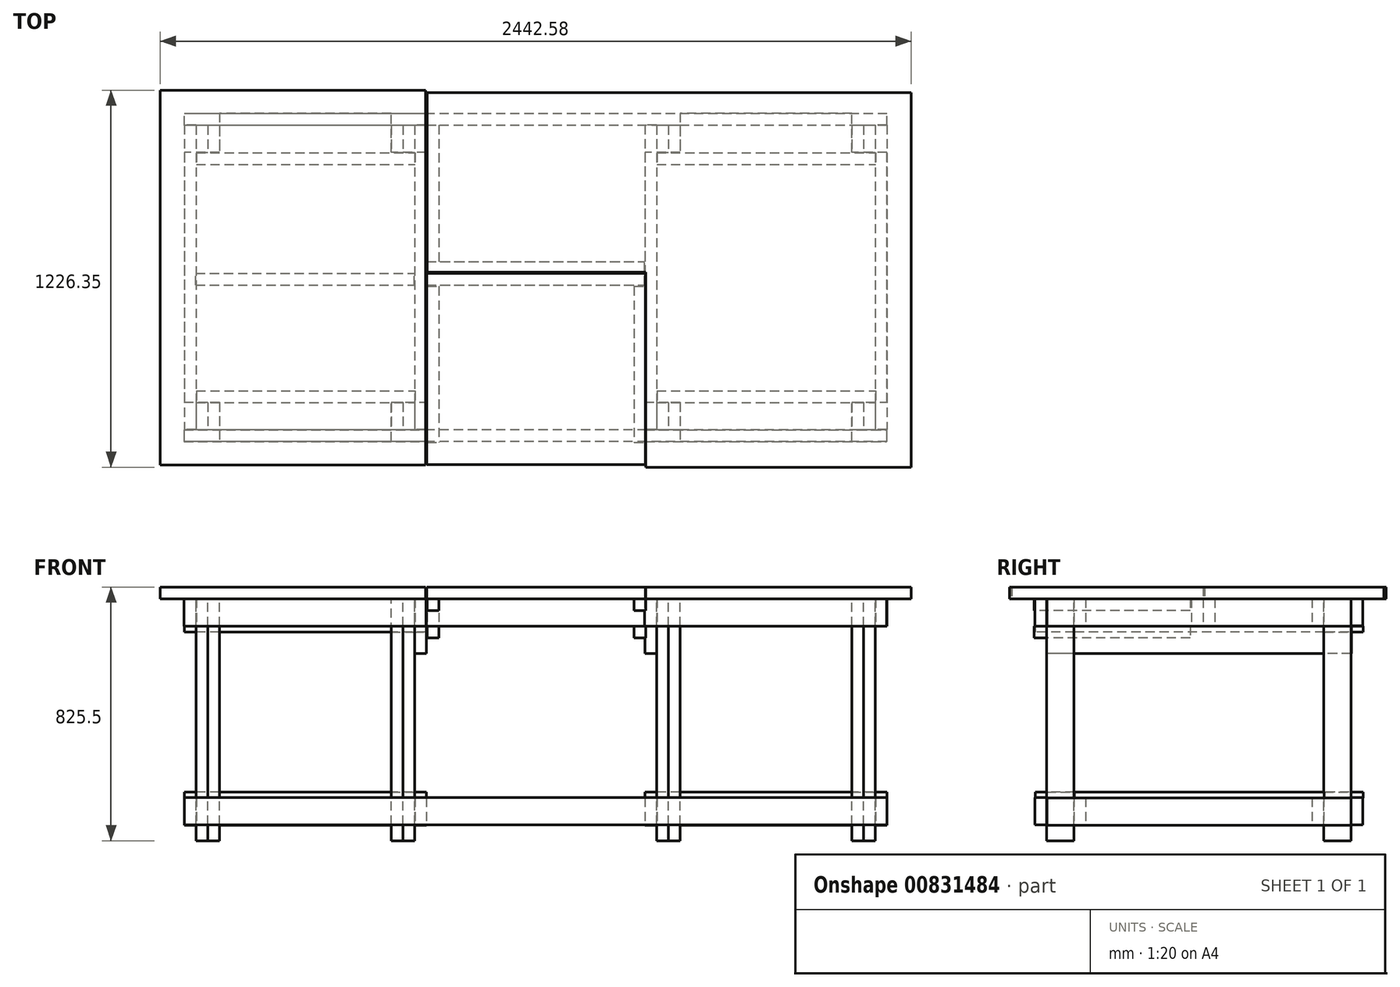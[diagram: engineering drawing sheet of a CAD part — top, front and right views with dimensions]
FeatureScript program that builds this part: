
annotation { "Feature Type Name" : "Feature", "Feature Type Description" : "" }
export const myFeature = defineFeature(function(context is Context, id is Id, definition is map)
    precondition{}
    {
        {
            var Q0;
            Q0=qCreatedBy(makeId("Top.planeOp"),FACE);
            var sketch = newSketch(context, id + "F0", { "sketchPlane" : qUnion([Q0])});
            skLineSegment(sketch, "E0.bottom", {"start": v(-393.7, 19.05) * mm, "end": v(393.7, 19.05) * mm});
            skLineSegment(sketch, "E0.top", {"start": v(-393.7, -19.05) * mm, "end": v(393.7, -19.05) * mm});
            skLineSegment(sketch, "E0.left", {"start": v(-393.7, 19.05) * mm, "end": v(-393.7, -19.05) * mm});
            skLineSegment(sketch, "E0.right", {"start": v(393.7, 19.05) * mm, "end": v(393.7, -19.05) * mm});
            skPoint(sketch, "E0.middle", {"position": v(0, 0) * mm});
            skSolve(sketch);
        }
        {
            var Q0;
            Q0=makeQuery(id+"F0.imprint","IMPRINT",FACE,{"disambiguationData":[TD([[makeQuery(id+"F0.imprint","IMPRINT",EDGE,{"derivedFrom":sQuery(id+"F0.wireOp",EDGE,"E0.bottom")}),-1.0]])]});
            extrude(context, id + "F1", {"entities" : qUnion([Q0]), "depth" : 88.9 * mm, "offsetDistance" : 25.4 * mm});
        }
        {
            var Q0;
            Q0=makeQuery(id+"F1.opExtrude","SWEPT_BODY",BODY,{"disambiguationData":[OSD([sQuery(id+"F0.wireOp",EDGE,"E0.bottom"),sQuery(id+"F0.wireOp",EDGE,"E0.top"),sQuery(id+"F0.wireOp",EDGE,"E0.left"),sQuery(id+"F0.wireOp",EDGE,"E0.right")])]});
            var Q1;
            Q1=qCreatedBy(makeId("Front.planeOp"),FACE);
            transform(context, id + "F2", {"entities" : qUnion([Q0]), "transformType" : TransformType.TRANSLATION_DISTANCE, "transformDirection" : qUnion([Q1]), "distance" : 1028.7 * mm, "makeCopy" : true});
        }
        {
            var Q0;
            Q0=makeQuery(id+"F1.opExtrude","SWEPT_BODY",BODY,{"disambiguationData":[OSD([sQuery(id+"F0.wireOp",EDGE,"E0.bottom"),sQuery(id+"F0.wireOp",EDGE,"E0.top"),sQuery(id+"F0.wireOp",EDGE,"E0.left"),sQuery(id+"F0.wireOp",EDGE,"E0.right")])]});
            var Q1;
            Q1=makeQuery(id+"F1.opExtrude","SWEPT_FACE",FACE,{"disambiguationData":[OSD([sQuery(id+"F0.wireOp",EDGE,"E0.right")])]});
            transform(context, id + "F3", {"entities" : qUnion([Q0]), "transformType" : TransformType.TRANSLATION_DISTANCE, "transformDirection" : qUnion([Q1]), "distance" : 1498.6 * mm, "makeCopy" : true});
        }
        {
            var Q0;
            Q0=makeQuery(id+"F3.opPattern","COPY",EDGE,{"derivedFrom":makeQuery(id+"F1.opExtrude","CAP_EDGE",EDGE,{"disambiguationData":[OSD([sQuery(id+"F0.wireOp",EDGE,"E0.top")])],"isStart":true}),"instanceName":"1"});
            cPoint(context, id + "F4", {"entities" : qUnion([Q0]), "parameter" : 0.5});
        }
        {
            var Q0;
            Q0=makeQuery(id+"F3.opPattern","COPY",BODY,{"derivedFrom":makeQuery(id+"F1.opExtrude","SWEPT_BODY",BODY,{"disambiguationData":[OSD([sQuery(id+"F0.wireOp",EDGE,"E0.bottom"),sQuery(id+"F0.wireOp",EDGE,"E0.top"),sQuery(id+"F0.wireOp",EDGE,"E0.left"),sQuery(id+"F0.wireOp",EDGE,"E0.right")])]}),"instanceName":"1"});
            var Q1;
            Q1 = qCreatedBy(id + "F4" ,VERTEX);
            var Q2;
            Q2=makeQuery(id+"F3.opPattern","COPY",EDGE,{"derivedFrom":makeQuery(id+"F1.opExtrude","CAP_EDGE",EDGE,{"disambiguationData":[OSD([sQuery(id+"F0.wireOp",EDGE,"E0.top")])],"isStart":false}),"instanceName":"1"});
            var Q3;
            Q3=makeQuery(id+"F3.opPattern","COPY",FACE,{"derivedFrom":makeQuery(id+"F1.opExtrude","SWEPT_FACE",FACE,{"disambiguationData":[OSD([sQuery(id+"F0.wireOp",EDGE,"E0.top")])]}),"instanceName":"1"});
            transform(context, id + "F5", {"entities" : qUnion([Q0]), "transformType" : TransformType.TRANSLATION_DISTANCE, "transformDirection" : qUnion([Q3]), "distance" : 1028.7 * mm, "makeCopy" : true});
        }
        {
            var Q0;
            Q0=qCreatedBy(makeId("Top.planeOp"),FACE);
            var sketch = newSketch(context, id + "F6", { "sketchPlane" : qUnion([Q0])});
            skLineSegment(sketch, "E1.bottom", {"start": v(1892.74, -19.08) * mm, "end": v(1854.64, -19.08) * mm});
            skLineSegment(sketch, "E1.top", {"start": v(1892.74, -107.98) * mm, "end": v(1854.64, -107.98) * mm});
            skLineSegment(sketch, "E1.left", {"start": v(1892.74, -19.08) * mm, "end": v(1892.74, -107.98) * mm});
            skLineSegment(sketch, "E1.right", {"start": v(1854.64, -19.08) * mm, "end": v(1854.64, -107.98) * mm});
            skSolve(sketch);
        }
        {
            var Q0;
            Q0=makeQuery(id+"F6.imprint","IMPRINT",FACE,{"disambiguationData":[TD([[makeQuery(id+"F6.imprint","IMPRINT",EDGE,{"derivedFrom":sQuery(id+"F6.wireOp",EDGE,"E1.bottom")}),1.0]])]});
            extrude(context, id + "F7", {"entities" : qUnion([Q0]), "oppositeDirection" : true, "depth" : 698.5 * mm, "offsetDistance" : 25.4 * mm, "hasSecondDirection" : true, "secondDirectionOppositeDirection" : false, "secondDirectionDepth" : 88.9 * mm});
        }
        {
            var Q0;
            Q0=makeQuery(id+"F7.opExtrude","SWEPT_BODY",BODY,{"disambiguationData":[OSD([sQuery(id+"F6.wireOp",EDGE,"E1.bottom"),sQuery(id+"F6.wireOp",EDGE,"E1.top"),sQuery(id+"F6.wireOp",EDGE,"E1.left"),sQuery(id+"F6.wireOp",EDGE,"E1.right")])]});
            var Q1;
            Q1=makeQuery(id+"F7.opExtrude","SWEPT_FACE",FACE,{"disambiguationData":[OSD([sQuery(id+"F6.wireOp",EDGE,"E1.top")])]});
            var Q2;
            Q2=makeQuery(id+"F7.opExtrude","SWEPT_FACE",FACE,{"disambiguationData":[OSD([sQuery(id+"F6.wireOp",EDGE,"E1.left")])]});
            transform(context, id + "F8", {"entities" : qUnion([Q0]), "transformType" : TransformType.TRANSLATION_DISTANCE, "transformDirection" : qUnion([Q1, Q2]), "distance" : 901.7 * mm, "makeCopy" : true});
        }
        {
            var Q0;
            Q0=makeQuery(id+"F8.opPattern","COPY",BODY,{"derivedFrom":makeQuery(id+"F7.opExtrude","SWEPT_BODY",BODY,{"disambiguationData":[OSD([sQuery(id+"F6.wireOp",EDGE,"E1.bottom"),sQuery(id+"F6.wireOp",EDGE,"E1.top"),sQuery(id+"F6.wireOp",EDGE,"E1.left"),sQuery(id+"F6.wireOp",EDGE,"E1.right")])]}),"instanceName":"1"});
            var Q1;
            Q1=makeQuery(id+"F8.opPattern","COPY",FACE,{"derivedFrom":makeQuery(id+"F7.opExtrude","SWEPT_FACE",FACE,{"disambiguationData":[OSD([sQuery(id+"F6.wireOp",EDGE,"E1.right")])]}),"instanceName":"1"});
            transform(context, id + "F9", {"entities" : qUnion([Q0]), "transformType" : TransformType.TRANSLATION_DISTANCE, "transformDirection" : qUnion([Q1]), "distance" : 749.3 * mm, "makeCopy" : true});
        }
        {
            var Q0;
            Q0=makeQuery(id+"F7.opExtrude","SWEPT_BODY",BODY,{"disambiguationData":[OSD([sQuery(id+"F6.wireOp",EDGE,"E1.bottom"),sQuery(id+"F6.wireOp",EDGE,"E1.top"),sQuery(id+"F6.wireOp",EDGE,"E1.left"),sQuery(id+"F6.wireOp",EDGE,"E1.right")])]});
            var Q1;
            Q1=makeQuery(id+"F7.opExtrude","SWEPT_FACE",FACE,{"disambiguationData":[OSD([sQuery(id+"F6.wireOp",EDGE,"E1.right")])]});
            transform(context, id + "F10", {"entities" : qUnion([Q0]), "transformType" : TransformType.TRANSLATION_DISTANCE, "transformDirection" : qUnion([Q1]), "distance" : 749.3 * mm, "makeCopy" : true});
        }
        {
            var Q0;
            Q0=makeQuery(id+"F10.opPattern","COPY",BODY,{"derivedFrom":makeQuery(id+"F7.opExtrude","SWEPT_BODY",BODY,{"disambiguationData":[OSD([sQuery(id+"F6.wireOp",EDGE,"E1.bottom"),sQuery(id+"F6.wireOp",EDGE,"E1.top"),sQuery(id+"F6.wireOp",EDGE,"E1.left"),sQuery(id+"F6.wireOp",EDGE,"E1.right")])]}),"instanceName":"1"});
            var Q1;
            Q1=makeQuery(id+"F10.opPattern","COPY",FACE,{"derivedFrom":makeQuery(id+"F7.opExtrude","SWEPT_FACE",FACE,{"disambiguationData":[OSD([sQuery(id+"F6.wireOp",EDGE,"E1.right")])]}),"instanceName":"1"});
            transform(context, id + "F11", {"entities" : qUnion([Q0]), "transformType" : TransformType.TRANSLATION_DISTANCE, "transformDirection" : qUnion([Q1]), "distance" : 749.3 * mm, "makeCopy" : true});
        }
        {
            var Q0;
            Q0=makeQuery(id+"F9.opPattern","COPY",BODY,{"derivedFrom":makeQuery(id+"F8.opPattern","COPY",BODY,{"derivedFrom":makeQuery(id+"F7.opExtrude","SWEPT_BODY",BODY,{"disambiguationData":[OSD([sQuery(id+"F6.wireOp",EDGE,"E1.bottom"),sQuery(id+"F6.wireOp",EDGE,"E1.top"),sQuery(id+"F6.wireOp",EDGE,"E1.left"),sQuery(id+"F6.wireOp",EDGE,"E1.right")])]}),"instanceName":"1"}),"instanceName":"1"});
            var Q1;
            Q1=makeQuery(id+"F9.opPattern","COPY",FACE,{"derivedFrom":makeQuery(id+"F8.opPattern","COPY",FACE,{"derivedFrom":makeQuery(id+"F7.opExtrude","SWEPT_FACE",FACE,{"disambiguationData":[OSD([sQuery(id+"F6.wireOp",EDGE,"E1.right")])]}),"instanceName":"1"}),"instanceName":"1"});
            transform(context, id + "F12", {"entities" : qUnion([Q0]), "transformType" : TransformType.TRANSLATION_DISTANCE, "transformDirection" : qUnion([Q1]), "distance" : 749.3 * mm, "makeCopy" : true});
        }
        {
            var Q0;
            Q0=makeQuery(id+"F12.opPattern","COPY",BODY,{"derivedFrom":makeQuery(id+"F9.opPattern","COPY",BODY,{"derivedFrom":makeQuery(id+"F8.opPattern","COPY",BODY,{"derivedFrom":makeQuery(id+"F7.opExtrude","SWEPT_BODY",BODY,{"disambiguationData":[OSD([sQuery(id+"F6.wireOp",EDGE,"E1.bottom"),sQuery(id+"F6.wireOp",EDGE,"E1.top"),sQuery(id+"F6.wireOp",EDGE,"E1.left"),sQuery(id+"F6.wireOp",EDGE,"E1.right")])]}),"instanceName":"1"}),"instanceName":"1"}),"instanceName":"1"});
            var Q1;
            Q1=makeQuery(id+"F12.opPattern","COPY",FACE,{"derivedFrom":makeQuery(id+"F9.opPattern","COPY",FACE,{"derivedFrom":makeQuery(id+"F8.opPattern","COPY",FACE,{"derivedFrom":makeQuery(id+"F7.opExtrude","SWEPT_FACE",FACE,{"disambiguationData":[OSD([sQuery(id+"F6.wireOp",EDGE,"E1.right")])]}),"instanceName":"1"}),"instanceName":"1"}),"instanceName":"1"});
            transform(context, id + "F13", {"entities" : qUnion([Q0]), "transformType" : TransformType.TRANSLATION_DISTANCE, "transformDirection" : qUnion([Q1]), "distance" : 749.3 * mm, "makeCopy" : true});
        }
        {
            var Q0;
            Q0=makeQuery(id+"F11.opPattern","COPY",BODY,{"derivedFrom":makeQuery(id+"F10.opPattern","COPY",BODY,{"derivedFrom":makeQuery(id+"F7.opExtrude","SWEPT_BODY",BODY,{"disambiguationData":[OSD([sQuery(id+"F6.wireOp",EDGE,"E1.bottom"),sQuery(id+"F6.wireOp",EDGE,"E1.top"),sQuery(id+"F6.wireOp",EDGE,"E1.left"),sQuery(id+"F6.wireOp",EDGE,"E1.right")])]}),"instanceName":"1"}),"instanceName":"1"});
            var Q1;
            Q1=makeQuery(id+"F11.opPattern","COPY",FACE,{"derivedFrom":makeQuery(id+"F10.opPattern","COPY",FACE,{"derivedFrom":makeQuery(id+"F7.opExtrude","SWEPT_FACE",FACE,{"disambiguationData":[OSD([sQuery(id+"F6.wireOp",EDGE,"E1.right")])]}),"instanceName":"1"}),"instanceName":"1"});
            transform(context, id + "F14", {"entities" : qUnion([Q0]), "transformType" : TransformType.TRANSLATION_DISTANCE, "transformDirection" : qUnion([Q1]), "distance" : 749.3 * mm, "makeCopy" : true});
        }
        {
            var Q0;
            Q0=makeQuery(id+"F7.opExtrude","SWEPT_BODY",BODY,{"disambiguationData":[OSD([sQuery(id+"F6.wireOp",EDGE,"E1.bottom"),sQuery(id+"F6.wireOp",EDGE,"E1.top"),sQuery(id+"F6.wireOp",EDGE,"E1.left"),sQuery(id+"F6.wireOp",EDGE,"E1.right")])]});
            var Q1;
            Q1=makeQuery(id+"F7.opExtrude","SWEPT_FACE",FACE,{"disambiguationData":[OSD([sQuery(id+"F6.wireOp",EDGE,"E1.right")])]});
            transform(context, id + "F15", {"entities" : qUnion([Q0]), "transformType" : TransformType.TRANSLATION_DISTANCE, "transformDirection" : qUnion([Q1]), "distance" : 38.1 * mm, "makeCopy" : false});
        }
        {
            var Q0;
            Q0=makeQuery(id+"F8.opPattern","COPY",BODY,{"derivedFrom":makeQuery(id+"F7.opExtrude","SWEPT_BODY",BODY,{"disambiguationData":[OSD([sQuery(id+"F6.wireOp",EDGE,"E1.bottom"),sQuery(id+"F6.wireOp",EDGE,"E1.top"),sQuery(id+"F6.wireOp",EDGE,"E1.left"),sQuery(id+"F6.wireOp",EDGE,"E1.right")])]}),"instanceName":"1"});
            var Q1;
            Q1=makeQuery(id+"F8.opPattern","COPY",FACE,{"derivedFrom":makeQuery(id+"F7.opExtrude","SWEPT_FACE",FACE,{"disambiguationData":[OSD([sQuery(id+"F6.wireOp",EDGE,"E1.right")])]}),"instanceName":"1"});
            transform(context, id + "F16", {"entities" : qUnion([Q0]), "transformType" : TransformType.TRANSLATION_DISTANCE, "transformDirection" : qUnion([Q1]), "distance" : 38.1 * mm, "makeCopy" : false});
        }
        {
            var Q0;
            Q0=makeQuery(id+"F11.opPattern","COPY",BODY,{"derivedFrom":makeQuery(id+"F10.opPattern","COPY",BODY,{"derivedFrom":makeQuery(id+"F7.opExtrude","SWEPT_BODY",BODY,{"disambiguationData":[OSD([sQuery(id+"F6.wireOp",EDGE,"E1.bottom"),sQuery(id+"F6.wireOp",EDGE,"E1.top"),sQuery(id+"F6.wireOp",EDGE,"E1.left"),sQuery(id+"F6.wireOp",EDGE,"E1.right")])]}),"instanceName":"1"}),"instanceName":"1"});
            var Q1;
            Q1=makeQuery(id+"F11.opPattern","COPY",FACE,{"derivedFrom":makeQuery(id+"F10.opPattern","COPY",FACE,{"derivedFrom":makeQuery(id+"F7.opExtrude","SWEPT_FACE",FACE,{"disambiguationData":[OSD([sQuery(id+"F6.wireOp",EDGE,"E1.right")])]}),"instanceName":"1"}),"instanceName":"1"});
            transform(context, id + "F17", {"entities" : qUnion([Q0]), "transformType" : TransformType.TRANSLATION_DISTANCE, "transformDirection" : qUnion([Q1]), "distance" : 38.1 * mm, "makeCopy" : false});
        }
        {
            var Q0;
            Q0=makeQuery(id+"F12.opPattern","COPY",BODY,{"derivedFrom":makeQuery(id+"F9.opPattern","COPY",BODY,{"derivedFrom":makeQuery(id+"F8.opPattern","COPY",BODY,{"derivedFrom":makeQuery(id+"F7.opExtrude","SWEPT_BODY",BODY,{"disambiguationData":[OSD([sQuery(id+"F6.wireOp",EDGE,"E1.bottom"),sQuery(id+"F6.wireOp",EDGE,"E1.top"),sQuery(id+"F6.wireOp",EDGE,"E1.left"),sQuery(id+"F6.wireOp",EDGE,"E1.right")])]}),"instanceName":"1"}),"instanceName":"1"}),"instanceName":"1"});
            var Q1;
            Q1=makeQuery(id+"F12.opPattern","COPY",FACE,{"derivedFrom":makeQuery(id+"F9.opPattern","COPY",FACE,{"derivedFrom":makeQuery(id+"F8.opPattern","COPY",FACE,{"derivedFrom":makeQuery(id+"F7.opExtrude","SWEPT_FACE",FACE,{"disambiguationData":[OSD([sQuery(id+"F6.wireOp",EDGE,"E1.right")])]}),"instanceName":"1"}),"instanceName":"1"}),"instanceName":"1"});
            transform(context, id + "F18", {"entities" : qUnion([Q0]), "transformType" : TransformType.TRANSLATION_DISTANCE, "transformDirection" : qUnion([Q1]), "distance" : 38.1 * mm, "makeCopy" : false});
        }
        {
            var Q0;
            Q0=makeQuery(id+"F13.opPattern","COPY",BODY,{"derivedFrom":makeQuery(id+"F12.opPattern","COPY",BODY,{"derivedFrom":makeQuery(id+"F9.opPattern","COPY",BODY,{"derivedFrom":makeQuery(id+"F8.opPattern","COPY",BODY,{"derivedFrom":makeQuery(id+"F7.opExtrude","SWEPT_BODY",BODY,{"disambiguationData":[OSD([sQuery(id+"F6.wireOp",EDGE,"E1.bottom"),sQuery(id+"F6.wireOp",EDGE,"E1.top"),sQuery(id+"F6.wireOp",EDGE,"E1.left"),sQuery(id+"F6.wireOp",EDGE,"E1.right")])]}),"instanceName":"1"}),"instanceName":"1"}),"instanceName":"1"}),"instanceName":"1"});
            var Q1;
            Q1=makeQuery(id+"F13.opPattern","COPY",FACE,{"derivedFrom":makeQuery(id+"F12.opPattern","COPY",FACE,{"derivedFrom":makeQuery(id+"F9.opPattern","COPY",FACE,{"derivedFrom":makeQuery(id+"F8.opPattern","COPY",FACE,{"derivedFrom":makeQuery(id+"F7.opExtrude","SWEPT_FACE",FACE,{"disambiguationData":[OSD([sQuery(id+"F6.wireOp",EDGE,"E1.left")])]}),"instanceName":"1"}),"instanceName":"1"}),"instanceName":"1"}),"instanceName":"1"});
            transform(context, id + "F19", {"entities" : qUnion([Q0]), "transformType" : TransformType.TRANSLATION_DISTANCE, "transformDirection" : qUnion([Q1]), "distance" : 38.1 * mm, "makeCopy" : false});
        }
        {
            var Q0;
            Q0=makeQuery(id+"F14.opPattern","COPY",BODY,{"derivedFrom":makeQuery(id+"F11.opPattern","COPY",BODY,{"derivedFrom":makeQuery(id+"F10.opPattern","COPY",BODY,{"derivedFrom":makeQuery(id+"F7.opExtrude","SWEPT_BODY",BODY,{"disambiguationData":[OSD([sQuery(id+"F6.wireOp",EDGE,"E1.bottom"),sQuery(id+"F6.wireOp",EDGE,"E1.top"),sQuery(id+"F6.wireOp",EDGE,"E1.left"),sQuery(id+"F6.wireOp",EDGE,"E1.right")])]}),"instanceName":"1"}),"instanceName":"1"}),"instanceName":"1"});
            var Q1;
            Q1=makeQuery(id+"F14.opPattern","COPY",FACE,{"derivedFrom":makeQuery(id+"F11.opPattern","COPY",FACE,{"derivedFrom":makeQuery(id+"F10.opPattern","COPY",FACE,{"derivedFrom":makeQuery(id+"F7.opExtrude","SWEPT_FACE",FACE,{"disambiguationData":[OSD([sQuery(id+"F6.wireOp",EDGE,"E1.left")])]}),"instanceName":"1"}),"instanceName":"1"}),"instanceName":"1"});
            transform(context, id + "F20", {"entities" : qUnion([Q0]), "transformType" : TransformType.TRANSLATION_DISTANCE, "transformDirection" : qUnion([Q1]), "distance" : 38.1 * mm, "makeCopy" : false});
        }
        {
            var Q0;
            Q0=makeQuery(id+"F9.opPattern","COPY",BODY,{"derivedFrom":makeQuery(id+"F8.opPattern","COPY",BODY,{"derivedFrom":makeQuery(id+"F7.opExtrude","SWEPT_BODY",BODY,{"disambiguationData":[OSD([sQuery(id+"F6.wireOp",EDGE,"E1.bottom"),sQuery(id+"F6.wireOp",EDGE,"E1.top"),sQuery(id+"F6.wireOp",EDGE,"E1.left"),sQuery(id+"F6.wireOp",EDGE,"E1.right")])]}),"instanceName":"1"}),"instanceName":"1"});
            var Q1;
            Q1=makeQuery(id+"F9.opPattern","COPY",FACE,{"derivedFrom":makeQuery(id+"F8.opPattern","COPY",FACE,{"derivedFrom":makeQuery(id+"F7.opExtrude","SWEPT_FACE",FACE,{"disambiguationData":[OSD([sQuery(id+"F6.wireOp",EDGE,"E1.left")])]}),"instanceName":"1"}),"instanceName":"1"});
            transform(context, id + "F21", {"entities" : qUnion([Q0]), "transformType" : TransformType.TRANSLATION_DISTANCE, "transformDirection" : qUnion([Q1]), "distance" : 38.1 * mm, "makeCopy" : false});
        }
        {
            var Q0;
            Q0=makeQuery(id+"F10.opPattern","COPY",BODY,{"derivedFrom":makeQuery(id+"F7.opExtrude","SWEPT_BODY",BODY,{"disambiguationData":[OSD([sQuery(id+"F6.wireOp",EDGE,"E1.bottom"),sQuery(id+"F6.wireOp",EDGE,"E1.top"),sQuery(id+"F6.wireOp",EDGE,"E1.left"),sQuery(id+"F6.wireOp",EDGE,"E1.right")])]}),"instanceName":"1"});
            var Q1;
            Q1=makeQuery(id+"F10.opPattern","COPY",FACE,{"derivedFrom":makeQuery(id+"F7.opExtrude","SWEPT_FACE",FACE,{"disambiguationData":[OSD([sQuery(id+"F6.wireOp",EDGE,"E1.left")])]}),"instanceName":"1"});
            transform(context, id + "F22", {"entities" : qUnion([Q0]), "transformType" : TransformType.TRANSLATION_DISTANCE, "transformDirection" : qUnion([Q1]), "distance" : 38.1 * mm, "makeCopy" : false});
        }
        {
            var Q0;
            Q0=qCreatedBy(makeId("Top.planeOp"),FACE);
            var sketch = newSketch(context, id + "F23", { "sketchPlane" : qUnion([Q0])});
            skLineSegment(sketch, "E2.bottom", {"start": v(-354.84, -17.7) * mm, "end": v(-392.94, -17.7) * mm});
            skLineSegment(sketch, "E2.top", {"start": v(-354.84, -1008.3) * mm, "end": v(-392.94, -1008.3) * mm});
            skLineSegment(sketch, "E2.left", {"start": v(-354.84, -17.7) * mm, "end": v(-354.84, -1008.3) * mm});
            skLineSegment(sketch, "E2.right", {"start": v(-392.94, -17.7) * mm, "end": v(-392.94, -1008.3) * mm});
            skSolve(sketch);
        }
        {
            var Q0;
            Q0=makeQuery(id+"F23.imprint","IMPRINT",FACE,{"disambiguationData":[TD([[makeQuery(id+"F23.imprint","IMPRINT",EDGE,{"derivedFrom":sQuery(id+"F23.wireOp",EDGE,"E2.bottom")}),1.0]])]});
            extrude(context, id + "F24", {"entities" : qUnion([Q0]), "depth" : 88.9 * mm, "offsetDistance" : 25.4 * mm});
        }
        {
            var Q0;
            Q0=makeQuery(id+"F24.opExtrude","SWEPT_BODY",BODY,{"disambiguationData":[OSD([sQuery(id+"F23.wireOp",EDGE,"E2.bottom"),sQuery(id+"F23.wireOp",EDGE,"E2.top"),sQuery(id+"F23.wireOp",EDGE,"E2.left"),sQuery(id+"F23.wireOp",EDGE,"E2.right")])]});
            var Q1;
            Q1=makeQuery(id+"F24.opExtrude","SWEPT_FACE",FACE,{"disambiguationData":[OSD([sQuery(id+"F23.wireOp",EDGE,"E2.left")])]});
            transform(context, id + "F25", {"entities" : qUnion([Q0]), "transformType" : TransformType.TRANSLATION_DISTANCE, "transformDirection" : qUnion([Q1]), "distance" : 2247.9 * mm, "makeCopy" : true});
        }
        {
            var Q0;
            Q0=makeQuery(id+"F25.opPattern","COPY",BODY,{"derivedFrom":makeQuery(id+"F24.opExtrude","SWEPT_BODY",BODY,{"disambiguationData":[OSD([sQuery(id+"F23.wireOp",EDGE,"E2.bottom"),sQuery(id+"F23.wireOp",EDGE,"E2.top"),sQuery(id+"F23.wireOp",EDGE,"E2.left"),sQuery(id+"F23.wireOp",EDGE,"E2.right")])]}),"instanceName":"1"});
            var Q1;
            Q1=makeQuery(id+"F25.opPattern","COPY",FACE,{"derivedFrom":makeQuery(id+"F24.opExtrude","SWEPT_FACE",FACE,{"disambiguationData":[OSD([sQuery(id+"F23.wireOp",EDGE,"E2.right")])]}),"instanceName":"1"});
            transform(context, id + "F26", {"entities" : qUnion([Q0]), "transformType" : TransformType.TRANSLATION_DISTANCE, "transformDirection" : qUnion([Q1]), "distance" : 749.3 * mm, "makeCopy" : true});
        }
        {
            var Q0;
            Q0=makeQuery(id+"F26.opPattern","COPY",BODY,{"derivedFrom":makeQuery(id+"F25.opPattern","COPY",BODY,{"derivedFrom":makeQuery(id+"F24.opExtrude","SWEPT_BODY",BODY,{"disambiguationData":[OSD([sQuery(id+"F23.wireOp",EDGE,"E2.bottom"),sQuery(id+"F23.wireOp",EDGE,"E2.top"),sQuery(id+"F23.wireOp",EDGE,"E2.left"),sQuery(id+"F23.wireOp",EDGE,"E2.right")])]}),"instanceName":"1"}),"instanceName":"1"});
            var Q1;
            Q1=makeQuery(id+"F26.opPattern","COPY",FACE,{"derivedFrom":makeQuery(id+"F25.opPattern","COPY",FACE,{"derivedFrom":makeQuery(id+"F24.opExtrude","SWEPT_FACE",FACE,{"disambiguationData":[OSD([sQuery(id+"F23.wireOp",EDGE,"E2.right")])]}),"instanceName":"1"}),"instanceName":"1"});
            transform(context, id + "F27", {"entities" : qUnion([Q0]), "transformType" : TransformType.TRANSLATION_DISTANCE, "transformDirection" : qUnion([Q1]), "distance" : 749.3 * mm, "makeCopy" : true});
        }
        {
            var Q0;
            Q0=makeQuery(id+"F11.opPattern","COPY",BODY,{"derivedFrom":makeQuery(id+"F10.opPattern","COPY",BODY,{"derivedFrom":makeQuery(id+"F7.opExtrude","SWEPT_BODY",BODY,{"disambiguationData":[OSD([sQuery(id+"F6.wireOp",EDGE,"E1.bottom"),sQuery(id+"F6.wireOp",EDGE,"E1.top"),sQuery(id+"F6.wireOp",EDGE,"E1.left"),sQuery(id+"F6.wireOp",EDGE,"E1.right")])]}),"instanceName":"1"}),"instanceName":"1"});
            var Q1;
            Q1=makeQuery(id+"F11.opPattern","COPY",FACE,{"derivedFrom":makeQuery(id+"F10.opPattern","COPY",FACE,{"derivedFrom":makeQuery(id+"F7.opExtrude","SWEPT_FACE",FACE,{"disambiguationData":[OSD([sQuery(id+"F6.wireOp",EDGE,"E1.right")])]}),"instanceName":"1"}),"instanceName":"1"});
            transform(context, id + "F28", {"entities" : qUnion([Q0]), "transformType" : TransformType.TRANSLATION_DISTANCE, "transformDirection" : qUnion([Q1]), "distance" : 38.1 * mm, "makeCopy" : true});
        }
        {
            var Q0;
            Q0=makeQuery(id+"F12.opPattern","COPY",BODY,{"derivedFrom":makeQuery(id+"F9.opPattern","COPY",BODY,{"derivedFrom":makeQuery(id+"F8.opPattern","COPY",BODY,{"derivedFrom":makeQuery(id+"F7.opExtrude","SWEPT_BODY",BODY,{"disambiguationData":[OSD([sQuery(id+"F6.wireOp",EDGE,"E1.bottom"),sQuery(id+"F6.wireOp",EDGE,"E1.top"),sQuery(id+"F6.wireOp",EDGE,"E1.left"),sQuery(id+"F6.wireOp",EDGE,"E1.right")])]}),"instanceName":"1"}),"instanceName":"1"}),"instanceName":"1"});
            var Q1;
            Q1=makeQuery(id+"F12.opPattern","COPY",FACE,{"derivedFrom":makeQuery(id+"F9.opPattern","COPY",FACE,{"derivedFrom":makeQuery(id+"F8.opPattern","COPY",FACE,{"derivedFrom":makeQuery(id+"F7.opExtrude","SWEPT_FACE",FACE,{"disambiguationData":[OSD([sQuery(id+"F6.wireOp",EDGE,"E1.right")])]}),"instanceName":"1"}),"instanceName":"1"}),"instanceName":"1"});
            transform(context, id + "F29", {"entities" : qUnion([Q0]), "transformType" : TransformType.TRANSLATION_DISTANCE, "transformDirection" : qUnion([Q1]), "distance" : 38.1 * mm, "makeCopy" : true});
        }
        {
            var Q0;
            Q0=makeQuery(id+"F8.opPattern","COPY",BODY,{"derivedFrom":makeQuery(id+"F7.opExtrude","SWEPT_BODY",BODY,{"disambiguationData":[OSD([sQuery(id+"F6.wireOp",EDGE,"E1.bottom"),sQuery(id+"F6.wireOp",EDGE,"E1.top"),sQuery(id+"F6.wireOp",EDGE,"E1.left"),sQuery(id+"F6.wireOp",EDGE,"E1.right")])]}),"instanceName":"1"});
            var Q1;
            Q1=makeQuery(id+"F8.opPattern","COPY",FACE,{"derivedFrom":makeQuery(id+"F7.opExtrude","SWEPT_FACE",FACE,{"disambiguationData":[OSD([sQuery(id+"F6.wireOp",EDGE,"E1.right")])]}),"instanceName":"1"});
            transform(context, id + "F30", {"entities" : qUnion([Q0]), "transformType" : TransformType.TRANSLATION_DISTANCE, "transformDirection" : qUnion([Q1]), "distance" : 38.1 * mm, "makeCopy" : true});
        }
        {
            var Q0;
            Q0=makeQuery(id+"F7.opExtrude","SWEPT_BODY",BODY,{"disambiguationData":[OSD([sQuery(id+"F6.wireOp",EDGE,"E1.bottom"),sQuery(id+"F6.wireOp",EDGE,"E1.top"),sQuery(id+"F6.wireOp",EDGE,"E1.left"),sQuery(id+"F6.wireOp",EDGE,"E1.right")])]});
            var Q1;
            Q1=makeQuery(id+"F7.opExtrude","SWEPT_FACE",FACE,{"disambiguationData":[OSD([sQuery(id+"F6.wireOp",EDGE,"E1.right")])]});
            transform(context, id + "F31", {"entities" : qUnion([Q0]), "transformType" : TransformType.TRANSLATION_DISTANCE, "transformDirection" : qUnion([Q1]), "distance" : 38.1 * mm, "makeCopy" : true});
        }
        {
            var Q0;
            Q0=makeQuery(id+"F13.opPattern","COPY",BODY,{"derivedFrom":makeQuery(id+"F12.opPattern","COPY",BODY,{"derivedFrom":makeQuery(id+"F9.opPattern","COPY",BODY,{"derivedFrom":makeQuery(id+"F8.opPattern","COPY",BODY,{"derivedFrom":makeQuery(id+"F7.opExtrude","SWEPT_BODY",BODY,{"disambiguationData":[OSD([sQuery(id+"F6.wireOp",EDGE,"E1.bottom"),sQuery(id+"F6.wireOp",EDGE,"E1.top"),sQuery(id+"F6.wireOp",EDGE,"E1.left"),sQuery(id+"F6.wireOp",EDGE,"E1.right")])]}),"instanceName":"1"}),"instanceName":"1"}),"instanceName":"1"}),"instanceName":"1"});
            var Q1;
            Q1=makeQuery(id+"F13.opPattern","COPY",FACE,{"derivedFrom":makeQuery(id+"F12.opPattern","COPY",FACE,{"derivedFrom":makeQuery(id+"F9.opPattern","COPY",FACE,{"derivedFrom":makeQuery(id+"F8.opPattern","COPY",FACE,{"derivedFrom":makeQuery(id+"F7.opExtrude","SWEPT_FACE",FACE,{"disambiguationData":[OSD([sQuery(id+"F6.wireOp",EDGE,"E1.left")])]}),"instanceName":"1"}),"instanceName":"1"}),"instanceName":"1"}),"instanceName":"1"});
            transform(context, id + "F32", {"entities" : qUnion([Q0]), "transformType" : TransformType.TRANSLATION_DISTANCE, "transformDirection" : qUnion([Q1]), "distance" : 38.1 * mm, "makeCopy" : true});
        }
        {
            var Q0;
            Q0=makeQuery(id+"F14.opPattern","COPY",BODY,{"derivedFrom":makeQuery(id+"F11.opPattern","COPY",BODY,{"derivedFrom":makeQuery(id+"F10.opPattern","COPY",BODY,{"derivedFrom":makeQuery(id+"F7.opExtrude","SWEPT_BODY",BODY,{"disambiguationData":[OSD([sQuery(id+"F6.wireOp",EDGE,"E1.bottom"),sQuery(id+"F6.wireOp",EDGE,"E1.top"),sQuery(id+"F6.wireOp",EDGE,"E1.left"),sQuery(id+"F6.wireOp",EDGE,"E1.right")])]}),"instanceName":"1"}),"instanceName":"1"}),"instanceName":"1"});
            var Q1;
            Q1=makeQuery(id+"F14.opPattern","COPY",FACE,{"derivedFrom":makeQuery(id+"F11.opPattern","COPY",FACE,{"derivedFrom":makeQuery(id+"F10.opPattern","COPY",FACE,{"derivedFrom":makeQuery(id+"F7.opExtrude","SWEPT_FACE",FACE,{"disambiguationData":[OSD([sQuery(id+"F6.wireOp",EDGE,"E1.left")])]}),"instanceName":"1"}),"instanceName":"1"}),"instanceName":"1"});
            transform(context, id + "F33", {"entities" : qUnion([Q0]), "transformType" : TransformType.TRANSLATION_DISTANCE, "transformDirection" : qUnion([Q1]), "distance" : 38.1 * mm, "makeCopy" : true});
        }
        {
            var Q0;
            Q0=makeQuery(id+"F10.opPattern","COPY",BODY,{"derivedFrom":makeQuery(id+"F7.opExtrude","SWEPT_BODY",BODY,{"disambiguationData":[OSD([sQuery(id+"F6.wireOp",EDGE,"E1.bottom"),sQuery(id+"F6.wireOp",EDGE,"E1.top"),sQuery(id+"F6.wireOp",EDGE,"E1.left"),sQuery(id+"F6.wireOp",EDGE,"E1.right")])]}),"instanceName":"1"});
            var Q1;
            Q1=makeQuery(id+"F10.opPattern","COPY",FACE,{"derivedFrom":makeQuery(id+"F7.opExtrude","SWEPT_FACE",FACE,{"disambiguationData":[OSD([sQuery(id+"F6.wireOp",EDGE,"E1.left")])]}),"instanceName":"1"});
            transform(context, id + "F34", {"entities" : qUnion([Q0]), "transformType" : TransformType.TRANSLATION_DISTANCE, "transformDirection" : qUnion([Q1]), "distance" : 38.1 * mm, "makeCopy" : true});
        }
        {
            var Q0;
            Q0=makeQuery(id+"F9.opPattern","COPY",BODY,{"derivedFrom":makeQuery(id+"F8.opPattern","COPY",BODY,{"derivedFrom":makeQuery(id+"F7.opExtrude","SWEPT_BODY",BODY,{"disambiguationData":[OSD([sQuery(id+"F6.wireOp",EDGE,"E1.bottom"),sQuery(id+"F6.wireOp",EDGE,"E1.top"),sQuery(id+"F6.wireOp",EDGE,"E1.left"),sQuery(id+"F6.wireOp",EDGE,"E1.right")])]}),"instanceName":"1"}),"instanceName":"1"});
            var Q1;
            Q1=makeQuery(id+"F9.opPattern","COPY",FACE,{"derivedFrom":makeQuery(id+"F8.opPattern","COPY",FACE,{"derivedFrom":makeQuery(id+"F7.opExtrude","SWEPT_FACE",FACE,{"disambiguationData":[OSD([sQuery(id+"F6.wireOp",EDGE,"E1.left")])]}),"instanceName":"1"}),"instanceName":"1"});
            transform(context, id + "F35", {"entities" : qUnion([Q0]), "transformType" : TransformType.TRANSLATION_DISTANCE, "transformDirection" : qUnion([Q1]), "distance" : 38.1 * mm, "makeCopy" : true});
        }
        {
            var Q0;
            Q0=makeQuery(id+"F27.opPattern","COPY",BODY,{"derivedFrom":makeQuery(id+"F26.opPattern","COPY",BODY,{"derivedFrom":makeQuery(id+"F25.opPattern","COPY",BODY,{"derivedFrom":makeQuery(id+"F24.opExtrude","SWEPT_BODY",BODY,{"disambiguationData":[OSD([sQuery(id+"F23.wireOp",EDGE,"E2.bottom"),sQuery(id+"F23.wireOp",EDGE,"E2.top"),sQuery(id+"F23.wireOp",EDGE,"E2.left"),sQuery(id+"F23.wireOp",EDGE,"E2.right")])]}),"instanceName":"1"}),"instanceName":"1"}),"instanceName":"1"});
            var Q1;
            Q1=makeQuery(id+"F27.opPattern","COPY",FACE,{"derivedFrom":makeQuery(id+"F26.opPattern","COPY",FACE,{"derivedFrom":makeQuery(id+"F25.opPattern","COPY",FACE,{"derivedFrom":makeQuery(id+"F24.opExtrude","CAP_FACE",FACE,{"disambiguationData":[OSD([sQuery(id+"F23.wireOp",EDGE,"E2.bottom"),sQuery(id+"F23.wireOp",EDGE,"E2.top"),sQuery(id+"F23.wireOp",EDGE,"E2.left"),sQuery(id+"F23.wireOp",EDGE,"E2.right")])],"isStart":true}),"instanceName":"1"}),"instanceName":"1"}),"instanceName":"1"});
            transform(context, id + "F36", {"entities" : qUnion([Q0]), "transformType" : TransformType.TRANSLATION_DISTANCE, "transformDirection" : qUnion([Q1]), "distance" : 647.7 * mm, "makeCopy" : true});
        }
        {
            var Q0;
            Q0=makeQuery(id+"F36.opPattern","COPY",BODY,{"derivedFrom":makeQuery(id+"F27.opPattern","COPY",BODY,{"derivedFrom":makeQuery(id+"F26.opPattern","COPY",BODY,{"derivedFrom":makeQuery(id+"F25.opPattern","COPY",BODY,{"derivedFrom":makeQuery(id+"F24.opExtrude","SWEPT_BODY",BODY,{"disambiguationData":[OSD([sQuery(id+"F23.wireOp",EDGE,"E2.bottom"),sQuery(id+"F23.wireOp",EDGE,"E2.top"),sQuery(id+"F23.wireOp",EDGE,"E2.left"),sQuery(id+"F23.wireOp",EDGE,"E2.right")])]}),"instanceName":"1"}),"instanceName":"1"}),"instanceName":"1"}),"instanceName":"1"});
            var Q1;
            Q1=makeQuery(id+"F36.opPattern","COPY",FACE,{"derivedFrom":makeQuery(id+"F27.opPattern","COPY",FACE,{"derivedFrom":makeQuery(id+"F26.opPattern","COPY",FACE,{"derivedFrom":makeQuery(id+"F25.opPattern","COPY",FACE,{"derivedFrom":makeQuery(id+"F24.opExtrude","SWEPT_FACE",FACE,{"disambiguationData":[OSD([sQuery(id+"F23.wireOp",EDGE,"E2.left")])]}),"instanceName":"1"}),"instanceName":"1"}),"instanceName":"1"}),"instanceName":"1"});
            transform(context, id + "F37", {"entities" : qUnion([Q0]), "transformType" : TransformType.TRANSLATION_DISTANCE, "transformDirection" : qUnion([Q1]), "distance" : 749.3 * mm, "makeCopy" : true});
        }
        {
            var Q0;
            Q0=makeQuery(id+"F37.opPattern","COPY",BODY,{"derivedFrom":makeQuery(id+"F36.opPattern","COPY",BODY,{"derivedFrom":makeQuery(id+"F27.opPattern","COPY",BODY,{"derivedFrom":makeQuery(id+"F26.opPattern","COPY",BODY,{"derivedFrom":makeQuery(id+"F25.opPattern","COPY",BODY,{"derivedFrom":makeQuery(id+"F24.opExtrude","SWEPT_BODY",BODY,{"disambiguationData":[OSD([sQuery(id+"F23.wireOp",EDGE,"E2.bottom"),sQuery(id+"F23.wireOp",EDGE,"E2.top"),sQuery(id+"F23.wireOp",EDGE,"E2.left"),sQuery(id+"F23.wireOp",EDGE,"E2.right")])]}),"instanceName":"1"}),"instanceName":"1"}),"instanceName":"1"}),"instanceName":"1"}),"instanceName":"1"});
            var Q1;
            Q1=makeQuery(id+"F37.opPattern","COPY",FACE,{"derivedFrom":makeQuery(id+"F36.opPattern","COPY",FACE,{"derivedFrom":makeQuery(id+"F27.opPattern","COPY",FACE,{"derivedFrom":makeQuery(id+"F26.opPattern","COPY",FACE,{"derivedFrom":makeQuery(id+"F25.opPattern","COPY",FACE,{"derivedFrom":makeQuery(id+"F24.opExtrude","SWEPT_FACE",FACE,{"disambiguationData":[OSD([sQuery(id+"F23.wireOp",EDGE,"E2.left")])]}),"instanceName":"1"}),"instanceName":"1"}),"instanceName":"1"}),"instanceName":"1"}),"instanceName":"1"});
            transform(context, id + "F38", {"entities" : qUnion([Q0]), "transformType" : TransformType.TRANSLATION_DISTANCE, "transformDirection" : qUnion([Q1]), "distance" : 749.3 * mm, "makeCopy" : true});
        }
        {
            var Q0;
            Q0=makeQuery(id+"F36.opPattern","COPY",BODY,{"derivedFrom":makeQuery(id+"F27.opPattern","COPY",BODY,{"derivedFrom":makeQuery(id+"F26.opPattern","COPY",BODY,{"derivedFrom":makeQuery(id+"F25.opPattern","COPY",BODY,{"derivedFrom":makeQuery(id+"F24.opExtrude","SWEPT_BODY",BODY,{"disambiguationData":[OSD([sQuery(id+"F23.wireOp",EDGE,"E2.bottom"),sQuery(id+"F23.wireOp",EDGE,"E2.top"),sQuery(id+"F23.wireOp",EDGE,"E2.left"),sQuery(id+"F23.wireOp",EDGE,"E2.right")])]}),"instanceName":"1"}),"instanceName":"1"}),"instanceName":"1"}),"instanceName":"1"});
            var Q1;
            Q1=makeQuery(id+"F36.opPattern","COPY",FACE,{"derivedFrom":makeQuery(id+"F27.opPattern","COPY",FACE,{"derivedFrom":makeQuery(id+"F26.opPattern","COPY",FACE,{"derivedFrom":makeQuery(id+"F25.opPattern","COPY",FACE,{"derivedFrom":makeQuery(id+"F24.opExtrude","SWEPT_FACE",FACE,{"disambiguationData":[OSD([sQuery(id+"F23.wireOp",EDGE,"E2.right")])]}),"instanceName":"1"}),"instanceName":"1"}),"instanceName":"1"}),"instanceName":"1"});
            transform(context, id + "F39", {"entities" : qUnion([Q0]), "transformType" : TransformType.TRANSLATION_DISTANCE, "transformDirection" : qUnion([Q1]), "distance" : 749.3 * mm, "makeCopy" : true});
        }
        {
            var Q0;
            Q0=qCreatedBy(makeId("Front.planeOp"),FACE);
            var sketch = newSketch(context, id + "F40", { "sketchPlane" : qUnion([Q0])});
            skLineSegment(sketch, "E3.bottom", {"start": v(1893.65, -557.61) * mm, "end": v(-392.35, -557.61) * mm});
            skLineSegment(sketch, "E3.top", {"start": v(1893.65, -646.51) * mm, "end": v(-392.35, -646.51) * mm});
            skLineSegment(sketch, "E3.left", {"start": v(1893.65, -557.61) * mm, "end": v(1893.65, -646.51) * mm});
            skLineSegment(sketch, "E3.right", {"start": v(-392.35, -557.61) * mm, "end": v(-392.35, -646.51) * mm});
            skSolve(sketch);
        }
        {
            var Q0;
            Q0=makeQuery(id+"F40.imprint","IMPRINT",FACE,{"disambiguationData":[TD([[makeQuery(id+"F40.imprint","IMPRINT",EDGE,{"derivedFrom":sQuery(id+"F40.wireOp",EDGE,"E3.bottom")}),1.0]])]});
            extrude(context, id + "F41", {"entities" : qUnion([Q0]), "endBound" : BoundingType.SYMMETRIC, "depth" : 38.1 * mm, "offsetDistance" : 25.4 * mm});
        }
        {
            var Q0;
            Q0=makeQuery(id+"F41.opExtrude","SWEPT_BODY",BODY,{"disambiguationData":[OSD([sQuery(id+"F40.wireOp",EDGE,"E3.bottom"),sQuery(id+"F40.wireOp",EDGE,"E3.top"),sQuery(id+"F40.wireOp",EDGE,"E3.left"),sQuery(id+"F40.wireOp",EDGE,"E3.right")])]});
            var Q1;
            Q1=makeQuery(id+"F41.opExtrude","CAP_FACE",FACE,{"disambiguationData":[OSD([sQuery(id+"F40.wireOp",EDGE,"E3.bottom"),sQuery(id+"F40.wireOp",EDGE,"E3.top"),sQuery(id+"F40.wireOp",EDGE,"E3.left"),sQuery(id+"F40.wireOp",EDGE,"E3.right")])],"isStart":false});
            transform(context, id + "F42", {"entities" : qUnion([Q0]), "transformType" : TransformType.TRANSLATION_DISTANCE, "transformDirection" : qUnion([Q1]), "distance" : 1028.7 * mm, "makeCopy" : true});
        }
        {
            var Q0;
            Q0=qCreatedBy(makeId("Top.planeOp"),FACE);
            var sketch = newSketch(context, id + "F43", { "sketchPlane" : qUnion([Q0])});
            skLineSegment(sketch, "E4.bottom", {"start": v(393.4, -1046.56) * mm, "end": v(1104.6, -1046.56) * mm});
            skLineSegment(sketch, "E4.top", {"start": v(393.4, -1008.46) * mm, "end": v(1104.6, -1008.46) * mm});
            skLineSegment(sketch, "E4.left", {"start": v(393.4, -1046.56) * mm, "end": v(393.4, -1008.46) * mm});
            skLineSegment(sketch, "E4.right", {"start": v(1104.6, -1046.56) * mm, "end": v(1104.6, -1008.46) * mm});
            skSolve(sketch);
        }
        {
            var Q0;
            Q0=makeQuery(id+"F43.imprint","IMPRINT",FACE,{"disambiguationData":[TD([[makeQuery(id+"F43.imprint","IMPRINT",EDGE,{"derivedFrom":sQuery(id+"F43.wireOp",EDGE,"E4.bottom")}),1.0]])]});
            extrude(context, id + "F44", {"entities" : qUnion([Q0]), "depth" : 88.9 * mm, "offsetDistance" : 25.4 * mm});
        }
        {
            var Q0;
            Q0=makeQuery(id+"F44.opExtrude","SWEPT_BODY",BODY,{"disambiguationData":[OSD([sQuery(id+"F43.wireOp",EDGE,"E4.bottom"),sQuery(id+"F43.wireOp",EDGE,"E4.top"),sQuery(id+"F43.wireOp",EDGE,"E4.left"),sQuery(id+"F43.wireOp",EDGE,"E4.right")])]});
            var Q1;
            Q1=makeQuery(id+"F44.opExtrude","SWEPT_FACE",FACE,{"disambiguationData":[OSD([sQuery(id+"F43.wireOp",EDGE,"E4.top")])]});
            transform(context, id + "F45", {"entities" : qUnion([Q0]), "transformType" : TransformType.TRANSLATION_DISTANCE, "transformDirection" : qUnion([Q1]), "distance" : 508 * mm, "makeCopy" : false});
        }
        {
            var Q0;
            Q0=makeQuery(id+"F3.opPattern","COPY",BODY,{"derivedFrom":makeQuery(id+"F1.opExtrude","SWEPT_BODY",BODY,{"disambiguationData":[OSD([sQuery(id+"F0.wireOp",EDGE,"E0.bottom"),sQuery(id+"F0.wireOp",EDGE,"E0.top"),sQuery(id+"F0.wireOp",EDGE,"E0.left"),sQuery(id+"F0.wireOp",EDGE,"E0.right")])]}),"instanceName":"1"});
            deleteBodies(context, id + "F46", {"entities" : qUnion([Q0])});
        }
        {
            var Q0;
            Q0=makeQuery(id+"F1.opExtrude","SWEPT_BODY",BODY,{"disambiguationData":[OSD([sQuery(id+"F0.wireOp",EDGE,"E0.bottom"),sQuery(id+"F0.wireOp",EDGE,"E0.top"),sQuery(id+"F0.wireOp",EDGE,"E0.left"),sQuery(id+"F0.wireOp",EDGE,"E0.right")])]});
            deleteBodies(context, id + "F47", {"entities" : qUnion([Q0])});
        }
        {
            var Q0;
            Q0=makeQuery(id+"F41.opExtrude","SWEPT_BODY",BODY,{"disambiguationData":[OSD([sQuery(id+"F40.wireOp",EDGE,"E3.bottom"),sQuery(id+"F40.wireOp",EDGE,"E3.top"),sQuery(id+"F40.wireOp",EDGE,"E3.left"),sQuery(id+"F40.wireOp",EDGE,"E3.right")])]});
            var Q1;
            Q1=makeQuery(id+"F41.opExtrude","SWEPT_FACE",FACE,{"disambiguationData":[OSD([sQuery(id+"F40.wireOp",EDGE,"E3.bottom")])]});
            transform(context, id + "F48", {"entities" : qUnion([Q0]), "transformType" : TransformType.TRANSLATION_DISTANCE, "transformDirection" : qUnion([Q1]), "distance" : 647.7 * mm, "makeCopy" : true});
        }
        {
            var Q0;
            Q0=makeQuery(id+"F44.opExtrude","SWEPT_BODY",BODY,{"disambiguationData":[OSD([sQuery(id+"F43.wireOp",EDGE,"E4.bottom"),sQuery(id+"F43.wireOp",EDGE,"E4.top"),sQuery(id+"F43.wireOp",EDGE,"E4.left"),sQuery(id+"F43.wireOp",EDGE,"E4.right")])]});
            var Q1;
            Q1=makeQuery(id+"F44.opExtrude","CAP_FACE",FACE,{"disambiguationData":[OSD([sQuery(id+"F43.wireOp",EDGE,"E4.bottom"),sQuery(id+"F43.wireOp",EDGE,"E4.top"),sQuery(id+"F43.wireOp",EDGE,"E4.left"),sQuery(id+"F43.wireOp",EDGE,"E4.right")])],"isStart":true});
            transform(context, id + "F49", {"entities" : qUnion([Q0]), "transformType" : TransformType.TRANSLATION_DISTANCE, "transformDirection" : qUnion([Q1]), "distance" : 647.7 * mm, "makeCopy" : true});
        }
        {
            var Q0;
            Q0=makeQuery(id+"F49.opPattern","COPY",BODY,{"derivedFrom":makeQuery(id+"F44.opExtrude","SWEPT_BODY",BODY,{"disambiguationData":[OSD([sQuery(id+"F43.wireOp",EDGE,"E4.bottom"),sQuery(id+"F43.wireOp",EDGE,"E4.top"),sQuery(id+"F43.wireOp",EDGE,"E4.left"),sQuery(id+"F43.wireOp",EDGE,"E4.right")])]}),"instanceName":"1"});
            deleteBodies(context, id + "F50", {"entities" : qUnion([Q0])});
        }
        {
            var Q0;
            Q0=qCreatedBy(makeId("Top.planeOp"),FACE);
            var sketch = newSketch(context, id + "F51", { "sketchPlane" : qUnion([Q0])});
            skLineSegment(sketch, "E5.bottom", {"start": v(-353.9, -108.41) * mm, "end": v(357.3, -108.41) * mm});
            skLineSegment(sketch, "E5.top", {"start": v(-353.9, -146.51) * mm, "end": v(357.3, -146.51) * mm});
            skLineSegment(sketch, "E5.left", {"start": v(-353.9, -108.41) * mm, "end": v(-353.9, -146.51) * mm});
            skLineSegment(sketch, "E5.right", {"start": v(357.3, -108.41) * mm, "end": v(357.3, -146.51) * mm});
            skSolve(sketch);
        }
        {
            var Q0;
            Q0=makeQuery(id+"F51.imprint","IMPRINT",FACE,{"disambiguationData":[TD([[makeQuery(id+"F51.imprint","IMPRINT",EDGE,{"derivedFrom":sQuery(id+"F51.wireOp",EDGE,"E5.bottom")}),-1.0]])]});
            extrude(context, id + "F52", {"entities" : qUnion([Q0]), "depth" : 88.9 * mm, "offsetDistance" : 25.4 * mm});
        }
        {
            var Q0;
            Q0=makeQuery(id+"F52.opExtrude","SWEPT_BODY",BODY,{"disambiguationData":[OSD([sQuery(id+"F51.wireOp",EDGE,"E5.bottom"),sQuery(id+"F51.wireOp",EDGE,"E5.top"),sQuery(id+"F51.wireOp",EDGE,"E5.left"),sQuery(id+"F51.wireOp",EDGE,"E5.right")])]});
            var Q1;
            Q1=makeQuery(id+"F52.opExtrude","CAP_FACE",FACE,{"disambiguationData":[OSD([sQuery(id+"F51.wireOp",EDGE,"E5.bottom"),sQuery(id+"F51.wireOp",EDGE,"E5.top"),sQuery(id+"F51.wireOp",EDGE,"E5.left"),sQuery(id+"F51.wireOp",EDGE,"E5.right")])],"isStart":true});
            transform(context, id + "F53", {"entities" : qUnion([Q0]), "transformType" : TransformType.TRANSLATION_DISTANCE, "transformDirection" : qUnion([Q1]), "distance" : 647.7 * mm, "makeCopy" : true});
        }
        {
            var Q0;
            Q0=makeQuery(id+"F53.opPattern","COPY",BODY,{"derivedFrom":makeQuery(id+"F52.opExtrude","SWEPT_BODY",BODY,{"disambiguationData":[OSD([sQuery(id+"F51.wireOp",EDGE,"E5.bottom"),sQuery(id+"F51.wireOp",EDGE,"E5.top"),sQuery(id+"F51.wireOp",EDGE,"E5.left"),sQuery(id+"F51.wireOp",EDGE,"E5.right")])]}),"instanceName":"1"});
            var Q1;
            Q1=makeQuery(id+"F53.opPattern","COPY",FACE,{"derivedFrom":makeQuery(id+"F52.opExtrude","SWEPT_FACE",FACE,{"disambiguationData":[OSD([sQuery(id+"F51.wireOp",EDGE,"E5.top")])]}),"instanceName":"1"});
            transform(context, id + "F54", {"entities" : qUnion([Q0]), "transformType" : TransformType.TRANSLATION_DISTANCE, "transformDirection" : qUnion([Q1]), "distance" : 774.7 * mm, "makeCopy" : true});
        }
        {
            var Q0;
            Q0=makeQuery(id+"F54.opPattern","COPY",BODY,{"derivedFrom":makeQuery(id+"F53.opPattern","COPY",BODY,{"derivedFrom":makeQuery(id+"F52.opExtrude","SWEPT_BODY",BODY,{"disambiguationData":[OSD([sQuery(id+"F51.wireOp",EDGE,"E5.bottom"),sQuery(id+"F51.wireOp",EDGE,"E5.top"),sQuery(id+"F51.wireOp",EDGE,"E5.left"),sQuery(id+"F51.wireOp",EDGE,"E5.right")])]}),"instanceName":"1"}),"instanceName":"1"});
            var Q1;
            Q1=makeQuery(id+"F54.opPattern","COPY",FACE,{"derivedFrom":makeQuery(id+"F53.opPattern","COPY",FACE,{"derivedFrom":makeQuery(id+"F52.opExtrude","CAP_FACE",FACE,{"disambiguationData":[OSD([sQuery(id+"F51.wireOp",EDGE,"E5.bottom"),sQuery(id+"F51.wireOp",EDGE,"E5.top"),sQuery(id+"F51.wireOp",EDGE,"E5.left"),sQuery(id+"F51.wireOp",EDGE,"E5.right")])],"isStart":false}),"instanceName":"1"}),"instanceName":"1"});
            transform(context, id + "F55", {"entities" : qUnion([Q0]), "transformType" : TransformType.TRANSLATION_DISTANCE, "transformDirection" : qUnion([Q1]), "distance" : 647.7 * mm, "makeCopy" : true});
        }
        {
            var Q0;
            Q0=makeQuery(id+"F55.opPattern","COPY",BODY,{"derivedFrom":makeQuery(id+"F54.opPattern","COPY",BODY,{"derivedFrom":makeQuery(id+"F53.opPattern","COPY",BODY,{"derivedFrom":makeQuery(id+"F52.opExtrude","SWEPT_BODY",BODY,{"disambiguationData":[OSD([sQuery(id+"F51.wireOp",EDGE,"E5.bottom"),sQuery(id+"F51.wireOp",EDGE,"E5.top"),sQuery(id+"F51.wireOp",EDGE,"E5.left"),sQuery(id+"F51.wireOp",EDGE,"E5.right")])]}),"instanceName":"1"}),"instanceName":"1"}),"instanceName":"1"});
            var Q1;
            Q1=makeQuery(id+"F26.opPattern","COPY",FACE,{"derivedFrom":makeQuery(id+"F25.opPattern","COPY",FACE,{"derivedFrom":makeQuery(id+"F24.opExtrude","SWEPT_FACE",FACE,{"disambiguationData":[OSD([sQuery(id+"F23.wireOp",EDGE,"E2.left")])]}),"instanceName":"1"}),"instanceName":"1"});
            transform(context, id + "F56", {"entities" : qUnion([Q0]), "transformType" : TransformType.TRANSLATION_DISTANCE, "transformDirection" : qUnion([Q1]), "distance" : 1498.6 * mm, "makeCopy" : true});
        }
        {
            var Q0;
            Q0=makeQuery(id+"F56.opPattern","COPY",BODY,{"derivedFrom":makeQuery(id+"F55.opPattern","COPY",BODY,{"derivedFrom":makeQuery(id+"F54.opPattern","COPY",BODY,{"derivedFrom":makeQuery(id+"F53.opPattern","COPY",BODY,{"derivedFrom":makeQuery(id+"F52.opExtrude","SWEPT_BODY",BODY,{"disambiguationData":[OSD([sQuery(id+"F51.wireOp",EDGE,"E5.bottom"),sQuery(id+"F51.wireOp",EDGE,"E5.top"),sQuery(id+"F51.wireOp",EDGE,"E5.left"),sQuery(id+"F51.wireOp",EDGE,"E5.right")])]}),"instanceName":"1"}),"instanceName":"1"}),"instanceName":"1"}),"instanceName":"1"});
            var Q1;
            Q1=makeQuery(id+"F56.opPattern","COPY",FACE,{"derivedFrom":makeQuery(id+"F55.opPattern","COPY",FACE,{"derivedFrom":makeQuery(id+"F54.opPattern","COPY",FACE,{"derivedFrom":makeQuery(id+"F53.opPattern","COPY",FACE,{"derivedFrom":makeQuery(id+"F52.opExtrude","CAP_FACE",FACE,{"disambiguationData":[OSD([sQuery(id+"F51.wireOp",EDGE,"E5.bottom"),sQuery(id+"F51.wireOp",EDGE,"E5.top"),sQuery(id+"F51.wireOp",EDGE,"E5.left"),sQuery(id+"F51.wireOp",EDGE,"E5.right")])],"isStart":true}),"instanceName":"1"}),"instanceName":"1"}),"instanceName":"1"}),"instanceName":"1"});
            transform(context, id + "F57", {"entities" : qUnion([Q0]), "transformType" : TransformType.TRANSLATION_DISTANCE, "transformDirection" : qUnion([Q1]), "distance" : 647.7 * mm, "makeCopy" : true});
        }
        {
            var Q0;
            Q0=makeQuery(id+"F57.opPattern","COPY",BODY,{"derivedFrom":makeQuery(id+"F56.opPattern","COPY",BODY,{"derivedFrom":makeQuery(id+"F55.opPattern","COPY",BODY,{"derivedFrom":makeQuery(id+"F54.opPattern","COPY",BODY,{"derivedFrom":makeQuery(id+"F53.opPattern","COPY",BODY,{"derivedFrom":makeQuery(id+"F52.opExtrude","SWEPT_BODY",BODY,{"disambiguationData":[OSD([sQuery(id+"F51.wireOp",EDGE,"E5.bottom"),sQuery(id+"F51.wireOp",EDGE,"E5.top"),sQuery(id+"F51.wireOp",EDGE,"E5.left"),sQuery(id+"F51.wireOp",EDGE,"E5.right")])]}),"instanceName":"1"}),"instanceName":"1"}),"instanceName":"1"}),"instanceName":"1"}),"instanceName":"1"});
            var Q1;
            Q1=makeQuery(id+"F57.opPattern","COPY",FACE,{"derivedFrom":makeQuery(id+"F56.opPattern","COPY",FACE,{"derivedFrom":makeQuery(id+"F55.opPattern","COPY",FACE,{"derivedFrom":makeQuery(id+"F54.opPattern","COPY",FACE,{"derivedFrom":makeQuery(id+"F53.opPattern","COPY",FACE,{"derivedFrom":makeQuery(id+"F52.opExtrude","SWEPT_FACE",FACE,{"disambiguationData":[OSD([sQuery(id+"F51.wireOp",EDGE,"E5.bottom")])]}),"instanceName":"1"}),"instanceName":"1"}),"instanceName":"1"}),"instanceName":"1"}),"instanceName":"1"});
            transform(context, id + "F58", {"entities" : qUnion([Q0]), "transformType" : TransformType.TRANSLATION_DISTANCE, "transformDirection" : qUnion([Q1]), "distance" : 774.7 * mm, "makeCopy" : true});
        }
        {
            var Q0;
            Q0=makeQuery(id+"F58.opPattern","COPY",BODY,{"derivedFrom":makeQuery(id+"F57.opPattern","COPY",BODY,{"derivedFrom":makeQuery(id+"F56.opPattern","COPY",BODY,{"derivedFrom":makeQuery(id+"F55.opPattern","COPY",BODY,{"derivedFrom":makeQuery(id+"F54.opPattern","COPY",BODY,{"derivedFrom":makeQuery(id+"F53.opPattern","COPY",BODY,{"derivedFrom":makeQuery(id+"F52.opExtrude","SWEPT_BODY",BODY,{"disambiguationData":[OSD([sQuery(id+"F51.wireOp",EDGE,"E5.bottom"),sQuery(id+"F51.wireOp",EDGE,"E5.top"),sQuery(id+"F51.wireOp",EDGE,"E5.left"),sQuery(id+"F51.wireOp",EDGE,"E5.right")])]}),"instanceName":"1"}),"instanceName":"1"}),"instanceName":"1"}),"instanceName":"1"}),"instanceName":"1"}),"instanceName":"1"});
            var Q1;
            Q1=makeQuery(id+"F58.opPattern","COPY",FACE,{"derivedFrom":makeQuery(id+"F57.opPattern","COPY",FACE,{"derivedFrom":makeQuery(id+"F56.opPattern","COPY",FACE,{"derivedFrom":makeQuery(id+"F55.opPattern","COPY",FACE,{"derivedFrom":makeQuery(id+"F54.opPattern","COPY",FACE,{"derivedFrom":makeQuery(id+"F53.opPattern","COPY",FACE,{"derivedFrom":makeQuery(id+"F52.opExtrude","CAP_FACE",FACE,{"disambiguationData":[OSD([sQuery(id+"F51.wireOp",EDGE,"E5.bottom"),sQuery(id+"F51.wireOp",EDGE,"E5.top"),sQuery(id+"F51.wireOp",EDGE,"E5.left"),sQuery(id+"F51.wireOp",EDGE,"E5.right")])],"isStart":false}),"instanceName":"1"}),"instanceName":"1"}),"instanceName":"1"}),"instanceName":"1"}),"instanceName":"1"}),"instanceName":"1"});
            transform(context, id + "F59", {"entities" : qUnion([Q0]), "transformType" : TransformType.TRANSLATION_DISTANCE, "transformDirection" : qUnion([Q1]), "distance" : 647.7 * mm, "makeCopy" : true});
        }
        {
            var Q0;
            Q0=makeQuery(id+"F44.opExtrude","SWEPT_BODY",BODY,{"disambiguationData":[OSD([sQuery(id+"F43.wireOp",EDGE,"E4.bottom"),sQuery(id+"F43.wireOp",EDGE,"E4.top"),sQuery(id+"F43.wireOp",EDGE,"E4.left"),sQuery(id+"F43.wireOp",EDGE,"E4.right")])]});
            var Q1;
            Q1=makeQuery(id+"F27.opPattern","COPY",FACE,{"derivedFrom":makeQuery(id+"F26.opPattern","COPY",FACE,{"derivedFrom":makeQuery(id+"F25.opPattern","COPY",FACE,{"derivedFrom":makeQuery(id+"F24.opExtrude","SWEPT_FACE",FACE,{"disambiguationData":[OSD([sQuery(id+"F23.wireOp",EDGE,"E2.right")])]}),"instanceName":"1"}),"instanceName":"1"}),"instanceName":"1"});
            transform(context, id + "F60", {"entities" : qUnion([Q0]), "transformType" : TransformType.TRANSLATION_DISTANCE, "transformDirection" : qUnion([Q1]), "distance" : 749.3 * mm, "makeCopy" : true});
        }
        {
            var Q0;
            Q0=makeQuery(id+"F27.opPattern","COPY",BODY,{"derivedFrom":makeQuery(id+"F26.opPattern","COPY",BODY,{"derivedFrom":makeQuery(id+"F25.opPattern","COPY",BODY,{"derivedFrom":makeQuery(id+"F24.opExtrude","SWEPT_BODY",BODY,{"disambiguationData":[OSD([sQuery(id+"F23.wireOp",EDGE,"E2.bottom"),sQuery(id+"F23.wireOp",EDGE,"E2.top"),sQuery(id+"F23.wireOp",EDGE,"E2.left"),sQuery(id+"F23.wireOp",EDGE,"E2.right")])]}),"instanceName":"1"}),"instanceName":"1"}),"instanceName":"1"});
            var Q1;
            Q1=makeQuery(id+"F27.opPattern","COPY",FACE,{"derivedFrom":makeQuery(id+"F26.opPattern","COPY",FACE,{"derivedFrom":makeQuery(id+"F25.opPattern","COPY",FACE,{"derivedFrom":makeQuery(id+"F24.opExtrude","CAP_FACE",FACE,{"disambiguationData":[OSD([sQuery(id+"F23.wireOp",EDGE,"E2.bottom"),sQuery(id+"F23.wireOp",EDGE,"E2.top"),sQuery(id+"F23.wireOp",EDGE,"E2.left"),sQuery(id+"F23.wireOp",EDGE,"E2.right")])],"isStart":true}),"instanceName":"1"}),"instanceName":"1"}),"instanceName":"1"});
            transform(context, id + "F61", {"entities" : qUnion([Q0]), "transformType" : TransformType.TRANSLATION_DISTANCE, "transformDirection" : qUnion([Q1]), "distance" : 88.9 * mm, "makeCopy" : true});
        }
        {
            var Q0;
            Q0=makeQuery(id+"F26.opPattern","COPY",BODY,{"derivedFrom":makeQuery(id+"F25.opPattern","COPY",BODY,{"derivedFrom":makeQuery(id+"F24.opExtrude","SWEPT_BODY",BODY,{"disambiguationData":[OSD([sQuery(id+"F23.wireOp",EDGE,"E2.bottom"),sQuery(id+"F23.wireOp",EDGE,"E2.top"),sQuery(id+"F23.wireOp",EDGE,"E2.left"),sQuery(id+"F23.wireOp",EDGE,"E2.right")])]}),"instanceName":"1"}),"instanceName":"1"});
            var Q1;
            Q1=makeQuery(id+"F26.opPattern","COPY",FACE,{"derivedFrom":makeQuery(id+"F25.opPattern","COPY",FACE,{"derivedFrom":makeQuery(id+"F24.opExtrude","CAP_FACE",FACE,{"disambiguationData":[OSD([sQuery(id+"F23.wireOp",EDGE,"E2.bottom"),sQuery(id+"F23.wireOp",EDGE,"E2.top"),sQuery(id+"F23.wireOp",EDGE,"E2.left"),sQuery(id+"F23.wireOp",EDGE,"E2.right")])],"isStart":true}),"instanceName":"1"}),"instanceName":"1"});
            transform(context, id + "F62", {"entities" : qUnion([Q0]), "transformType" : TransformType.TRANSLATION_DISTANCE, "transformDirection" : qUnion([Q1]), "distance" : 88.9 * mm, "makeCopy" : true});
        }
        {
            var Q0;
            Q0=qCreatedBy(makeId("Right.planeOp"),FACE);
            var sketch = newSketch(context, id + "F63", { "sketchPlane" : qUnion([Q0])});
            skLineSegment(sketch, "E6.bottom", {"start": v(-1177.45, 827.6) * mm, "end": v(-1647.35, 827.6) * mm});
            skLineSegment(sketch, "E6.top", {"start": v(-1177.45, 789.5) * mm, "end": v(-1647.35, 789.5) * mm});
            skLineSegment(sketch, "E6.left", {"start": v(-1177.45, 827.6) * mm, "end": v(-1177.45, 789.5) * mm});
            skLineSegment(sketch, "E6.right", {"start": v(-1647.35, 827.6) * mm, "end": v(-1647.35, 789.5) * mm});
            skSolve(sketch);
        }
        {
            var Q0;
            Q0 = qSketchRegion(id + "F63", true);
            extrude(context, id + "F64", {"entities" : qUnion([Q0]), "oppositeDirection" : true, "depth" : 38.1 * mm, "offsetDistance" : 25.4 * mm});
        }
        {
            var Q0;
            Q0=makeQuery(id+"F64.opExtrude","SWEPT_BODY",BODY,{"disambiguationData":[OSD([sQuery(id+"F63.wireOp",EDGE,"E6.bottom"),sQuery(id+"F63.wireOp",EDGE,"E6.top"),sQuery(id+"F63.wireOp",EDGE,"E6.left"),sQuery(id+"F63.wireOp",EDGE,"E6.right")])]});
            var Q1;
            Q1=makeQuery(id+"F64.opExtrude","CAP_FACE",FACE,{"disambiguationData":[OSD([sQuery(id+"F63.wireOp",EDGE,"E6.bottom"),sQuery(id+"F63.wireOp",EDGE,"E6.top"),sQuery(id+"F63.wireOp",EDGE,"E6.left"),sQuery(id+"F63.wireOp",EDGE,"E6.right")])],"isStart":false});
            transform(context, id + "F65", {"entities" : qUnion([Q0]), "transformType" : TransformType.TRANSLATION_DISTANCE, "transformDirection" : qUnion([Q1]), "distance" : 673.1 * mm, "makeCopy" : true});
        }
        {
            var Q0;
            Q0=makeQuery(id+"F64.opExtrude","SWEPT_BODY",BODY,{"disambiguationData":[OSD([sQuery(id+"F63.wireOp",EDGE,"E6.bottom"),sQuery(id+"F63.wireOp",EDGE,"E6.top"),sQuery(id+"F63.wireOp",EDGE,"E6.left"),sQuery(id+"F63.wireOp",EDGE,"E6.right")])]});
            var Q1;
            Q1=makeQuery(id+"F65.opPattern","COPY",BODY,{"derivedFrom":makeQuery(id+"F64.opExtrude","SWEPT_BODY",BODY,{"disambiguationData":[OSD([sQuery(id+"F63.wireOp",EDGE,"E6.bottom"),sQuery(id+"F63.wireOp",EDGE,"E6.top"),sQuery(id+"F63.wireOp",EDGE,"E6.left"),sQuery(id+"F63.wireOp",EDGE,"E6.right")])]}),"instanceName":"1"});
            deleteBodies(context, id + "F66", {"entities" : qUnion([Q0, Q1])});
        }
        {
            var Q0;
            Q0=qCreatedBy(makeId("Top.planeOp"),FACE);
            var sketch = newSketch(context, id + "F67", { "sketchPlane" : qUnion([Q0])});
            skLineSegment(sketch, "E7.bottom", {"start": v(397.63, -542.58) * mm, "end": v(435.73, -542.58) * mm});
            skLineSegment(sketch, "E7.top", {"start": v(397.63, -1050.58) * mm, "end": v(435.73, -1050.58) * mm});
            skLineSegment(sketch, "E7.left", {"start": v(397.63, -542.58) * mm, "end": v(397.63, -1050.58) * mm});
            skLineSegment(sketch, "E7.right", {"start": v(435.73, -542.58) * mm, "end": v(435.73, -1050.58) * mm});
            skSolve(sketch);
        }
        {
            var Q0;
            Q0=makeQuery(id+"F67.imprint","IMPRINT",FACE,{"disambiguationData":[TD([[makeQuery(id+"F67.imprint","IMPRINT",EDGE,{"derivedFrom":sQuery(id+"F67.wireOp",EDGE,"E7.bottom")}),-1.0]])]});
            extrude(context, id + "F68", {"entities" : qUnion([Q0]), "depth" : 38.1 * mm, "offsetDistance" : 25.4 * mm});
        }
        {
            var Q0;
            Q0=makeQuery(id+"F68.opExtrude","SWEPT_BODY",BODY,{"disambiguationData":[OSD([sQuery(id+"F67.wireOp",EDGE,"E7.bottom"),sQuery(id+"F67.wireOp",EDGE,"E7.top"),sQuery(id+"F67.wireOp",EDGE,"E7.left"),sQuery(id+"F67.wireOp",EDGE,"E7.right")])]});
            var Q1;
            Q1=makeQuery(id+"F68.opExtrude","CAP_FACE",FACE,{"disambiguationData":[OSD([sQuery(id+"F67.wireOp",EDGE,"E7.bottom"),sQuery(id+"F67.wireOp",EDGE,"E7.top"),sQuery(id+"F67.wireOp",EDGE,"E7.left"),sQuery(id+"F67.wireOp",EDGE,"E7.right")])],"isStart":false});
            transform(context, id + "F69", {"entities" : qUnion([Q0]), "transformType" : TransformType.TRANSLATION_DISTANCE, "transformDirection" : qUnion([Q1]), "distance" : 50.8 * mm, "makeCopy" : false});
        }
        {
            var Q0;
            Q0=makeQuery(id+"F68.opExtrude","SWEPT_BODY",BODY,{"disambiguationData":[OSD([sQuery(id+"F67.wireOp",EDGE,"E7.bottom"),sQuery(id+"F67.wireOp",EDGE,"E7.top"),sQuery(id+"F67.wireOp",EDGE,"E7.left"),sQuery(id+"F67.wireOp",EDGE,"E7.right")])]});
            var Q1;
            Q1=makeQuery(id+"F68.opExtrude","CAP_FACE",FACE,{"disambiguationData":[OSD([sQuery(id+"F67.wireOp",EDGE,"E7.bottom"),sQuery(id+"F67.wireOp",EDGE,"E7.top"),sQuery(id+"F67.wireOp",EDGE,"E7.left"),sQuery(id+"F67.wireOp",EDGE,"E7.right")])],"isStart":true});
            transform(context, id + "F70", {"entities" : qUnion([Q0]), "transformType" : TransformType.TRANSLATION_DISTANCE, "transformDirection" : qUnion([Q1]), "distance" : 88.9 * mm, "makeCopy" : true});
        }
        {
            var Q0;
            Q0=makeQuery(id+"F68.opExtrude","SWEPT_BODY",BODY,{"disambiguationData":[OSD([sQuery(id+"F67.wireOp",EDGE,"E7.bottom"),sQuery(id+"F67.wireOp",EDGE,"E7.top"),sQuery(id+"F67.wireOp",EDGE,"E7.left"),sQuery(id+"F67.wireOp",EDGE,"E7.right")])]});
            var Q1;
            Q1=makeQuery(id+"F68.opExtrude","SWEPT_FACE",FACE,{"disambiguationData":[OSD([sQuery(id+"F67.wireOp",EDGE,"E7.right")])]});
            transform(context, id + "F71", {"entities" : qUnion([Q0]), "transformType" : TransformType.TRANSLATION_DISTANCE, "transformDirection" : qUnion([Q1]), "distance" : 673.1 * mm, "makeCopy" : true});
        }
        {
            var Q0;
            Q0=makeQuery(id+"F70.opPattern","COPY",BODY,{"derivedFrom":makeQuery(id+"F68.opExtrude","SWEPT_BODY",BODY,{"disambiguationData":[OSD([sQuery(id+"F67.wireOp",EDGE,"E7.bottom"),sQuery(id+"F67.wireOp",EDGE,"E7.top"),sQuery(id+"F67.wireOp",EDGE,"E7.left"),sQuery(id+"F67.wireOp",EDGE,"E7.right")])]}),"instanceName":"1"});
            var Q1;
            Q1=makeQuery(id+"F70.opPattern","COPY",FACE,{"derivedFrom":makeQuery(id+"F68.opExtrude","SWEPT_FACE",FACE,{"disambiguationData":[OSD([sQuery(id+"F67.wireOp",EDGE,"E7.right")])]}),"instanceName":"1"});
            transform(context, id + "F72", {"entities" : qUnion([Q0]), "transformType" : TransformType.TRANSLATION_DISTANCE, "transformDirection" : qUnion([Q1]), "distance" : 673.1 * mm, "makeCopy" : true});
        }
        {
            var Q0;
            Q0=makeQuery(id+"F44.opExtrude","SWEPT_BODY",BODY,{"disambiguationData":[OSD([sQuery(id+"F43.wireOp",EDGE,"E4.bottom"),sQuery(id+"F43.wireOp",EDGE,"E4.top"),sQuery(id+"F43.wireOp",EDGE,"E4.left"),sQuery(id+"F43.wireOp",EDGE,"E4.right")])]});
            var Q1;
            Q1=makeQuery(id+"F44.opExtrude","SWEPT_FACE",FACE,{"disambiguationData":[OSD([sQuery(id+"F43.wireOp",EDGE,"E4.top")])]});
            transform(context, id + "F73", {"entities" : qUnion([Q0]), "transformType" : TransformType.TRANSLATION_DISTANCE, "transformDirection" : qUnion([Q1]), "distance" : 38.1 * mm, "makeCopy" : true});
        }
        {
            var Q0;
            Q0=qCreatedBy(makeId("Top.planeOp"),FACE);
            var sketch = newSketch(context, id + "F74", { "sketchPlane" : qUnion([Q0])});
            skLineSegment(sketch, "E8.bottom", {"start": v(396.74, -17.7) * mm, "end": v(434.84, -17.7) * mm});
            skLineSegment(sketch, "E8.top", {"start": v(396.74, -462.2) * mm, "end": v(434.84, -462.2) * mm});
            skLineSegment(sketch, "E8.left", {"start": v(396.74, -17.7) * mm, "end": v(396.74, -462.2) * mm});
            skLineSegment(sketch, "E8.right", {"start": v(434.84, -17.7) * mm, "end": v(434.84, -462.2) * mm});
            skSolve(sketch);
        }
        {
            var Q0;
            Q0 = qSketchRegion(id + "F74", true);
            extrude(context, id + "F75", {"entities" : qUnion([Q0]), "depth" : 88.9 * mm, "offsetDistance" : 25.4 * mm});
        }
        {
            var Q0;
            Q0=qCreatedBy(makeId("Top.planeOp"),FACE);
            var sketch = newSketch(context, id + "F76", { "sketchPlane" : qUnion([Q0])});
            skLineSegment(sketch, "E9.bottom", {"start": v(392.56, -1047.48) * mm, "end": v(-471.04, -1047.48) * mm});
            skLineSegment(sketch, "E9.top", {"start": v(392.56, 171.72) * mm, "end": v(-471.04, 171.72) * mm});
            skLineSegment(sketch, "E9.left", {"start": v(392.56, -1047.48) * mm, "end": v(392.56, 171.72) * mm});
            skLineSegment(sketch, "E9.right", {"start": v(-471.04, -1047.48) * mm, "end": v(-471.04, 171.72) * mm});
            skSolve(sketch);
        }
        {
            var Q0;
            Q0 = qSketchRegion(id + "F76", true);
            extrude(context, id + "F77", {"entities" : qUnion([Q0]), "depth" : 38.1 * mm, "offsetDistance" : 25.4 * mm});
        }
        {
            var Q0;
            Q0=makeQuery(id+"F77.opExtrude","SWEPT_BODY",BODY,{"disambiguationData":[OSD([sQuery(id+"F76.wireOp",EDGE,"E9.bottom"),sQuery(id+"F76.wireOp",EDGE,"E9.top"),sQuery(id+"F76.wireOp",EDGE,"E9.left"),sQuery(id+"F76.wireOp",EDGE,"E9.right")])]});
            var Q1;
            Q1=makeQuery(id+"F77.opExtrude","CAP_FACE",FACE,{"disambiguationData":[OSD([sQuery(id+"F76.wireOp",EDGE,"E9.bottom"),sQuery(id+"F76.wireOp",EDGE,"E9.top"),sQuery(id+"F76.wireOp",EDGE,"E9.left"),sQuery(id+"F76.wireOp",EDGE,"E9.right")])],"isStart":false});
            transform(context, id + "F78", {"entities" : qUnion([Q0]), "transformType" : TransformType.TRANSLATION_DISTANCE, "transformDirection" : qUnion([Q1]), "distance" : 88.9 * mm, "makeCopy" : false});
        }
        {
            var Q0;
            Q0=makeQuery(id+"F77.opExtrude","SWEPT_BODY",BODY,{"disambiguationData":[OSD([sQuery(id+"F76.wireOp",EDGE,"E9.bottom"),sQuery(id+"F76.wireOp",EDGE,"E9.top"),sQuery(id+"F76.wireOp",EDGE,"E9.left"),sQuery(id+"F76.wireOp",EDGE,"E9.right")])]});
            var Q1;
            Q1=makeQuery(id+"F77.opExtrude","SWEPT_FACE",FACE,{"disambiguationData":[OSD([sQuery(id+"F76.wireOp",EDGE,"E9.bottom")])]});
            transform(context, id + "F79", {"entities" : qUnion([Q0]), "transformType" : TransformType.TRANSLATION_DISTANCE, "transformDirection" : qUnion([Q1]), "distance" : 76.2 * mm, "makeCopy" : false});
        }
        {
            var Q0;
            Q0=makeQuery(id+"F71.opPattern","COPY",FACE,{"derivedFrom":makeQuery(id+"F68.opExtrude","CAP_FACE",FACE,{"disambiguationData":[OSD([sQuery(id+"F67.wireOp",EDGE,"E7.bottom"),sQuery(id+"F67.wireOp",EDGE,"E7.top"),sQuery(id+"F67.wireOp",EDGE,"E7.left"),sQuery(id+"F67.wireOp",EDGE,"E7.right")])],"isStart":false}),"instanceName":"1"});
            var sketch = newSketch(context, id + "F80", { "sketchPlane" : qUnion([Q0])});
            skLineSegment(sketch, "E10.bottom", {"start": v(1107.59, -500.5) * mm, "end": v(396.39, -500.5) * mm});
            skLineSegment(sketch, "E10.top", {"start": v(1107.59, -1122.8) * mm, "end": v(396.39, -1122.8) * mm});
            skLineSegment(sketch, "E10.left", {"start": v(1107.59, -500.5) * mm, "end": v(1107.59, -1122.8) * mm});
            skLineSegment(sketch, "E10.right", {"start": v(396.39, -500.5) * mm, "end": v(396.39, -1122.8) * mm});
            skSolve(sketch);
        }
        {
            var Q0;
            Q0 = qSketchRegion(id + "F80", true);
            extrude(context, id + "F81", {"entities" : qUnion([Q0]), "depth" : 38.1 * mm, "offsetDistance" : 25.4 * mm});
        }
        {
            var Q0;
            Q0=makeQuery(id+"F75.opExtrude","CAP_FACE",FACE,{"disambiguationData":[OSD([sQuery(id+"F74.wireOp",EDGE,"E8.bottom"),sQuery(id+"F74.wireOp",EDGE,"E8.top"),sQuery(id+"F74.wireOp",EDGE,"E8.left"),sQuery(id+"F74.wireOp",EDGE,"E8.right")])],"isStart":false});
            var sketch = newSketch(context, id + "F82", { "sketchPlane" : qUnion([Q0])});
            skLineSegment(sketch, "E11", {"start": v(1107.94, -495.83) * mm, "end": v(1107.94, -1130.83) * mm});
            skLineSegment(sketch, "E12", {"start": v(1107.94, -1130.83) * mm, "end": v(1971.54, -1130.83) * mm});
            skLineSegment(sketch, "E13", {"start": v(1971.54, -1130.83) * mm, "end": v(1971.54, 88.37) * mm});
            skLineSegment(sketch, "E14", {"start": v(1971.54, 88.37) * mm, "end": v(396.74, 88.37) * mm});
            skLineSegment(sketch, "E15", {"start": v(396.74, 88.37) * mm, "end": v(396.74, -495.83) * mm});
            skLineSegment(sketch, "E16", {"start": v(396.74, -495.83) * mm, "end": v(1107.94, -495.83) * mm});
            skSolve(sketch);
        }
        {
            var Q0;
            Q0 = qSketchRegion(id + "F82", true);
            extrude(context, id + "F83", {"entities" : qUnion([Q0]), "depth" : 38.1 * mm, "offsetDistance" : 25.4 * mm});
        }
        {
            var Q0;
            Q0=makeQuery(id+"F39.opPattern","COPY",FACE,{"derivedFrom":makeQuery(id+"F36.opPattern","COPY",FACE,{"derivedFrom":makeQuery(id+"F27.opPattern","COPY",FACE,{"derivedFrom":makeQuery(id+"F26.opPattern","COPY",FACE,{"derivedFrom":makeQuery(id+"F25.opPattern","COPY",FACE,{"derivedFrom":makeQuery(id+"F24.opExtrude","CAP_FACE",FACE,{"disambiguationData":[OSD([sQuery(id+"F23.wireOp",EDGE,"E2.bottom"),sQuery(id+"F23.wireOp",EDGE,"E2.top"),sQuery(id+"F23.wireOp",EDGE,"E2.left"),sQuery(id+"F23.wireOp",EDGE,"E2.right")])],"isStart":false}),"instanceName":"1"}),"instanceName":"1"}),"instanceName":"1"}),"instanceName":"1"}),"instanceName":"1"});
            var sketch = newSketch(context, id + "F84", { "sketchPlane" : qUnion([Q0])});
            skLineSegment(sketch, "E17", {"start": v(-278.64, -918.8) * mm, "end": v(-278.64, -1045.8) * mm});
            skLineSegment(sketch, "E18", {"start": v(-278.64, -1045.8) * mm, "end": v(280.16, -1045.8) * mm});
            skLineSegment(sketch, "E19", {"start": v(280.16, -1045.8) * mm, "end": v(280.16, -918.8) * mm});
            skLineSegment(sketch, "E20", {"start": v(280.16, -918.8) * mm, "end": v(394.46, -918.8) * mm});
            skLineSegment(sketch, "E21", {"start": v(394.46, -918.8) * mm, "end": v(394.46, -106) * mm});
            skLineSegment(sketch, "E22", {"start": v(394.46, -106) * mm, "end": v(280.16, -106) * mm});
            skLineSegment(sketch, "E23", {"start": v(280.16, -106) * mm, "end": v(280.16, 21) * mm});
            skLineSegment(sketch, "E24", {"start": v(280.16, 21) * mm, "end": v(-278.64, 21) * mm});
            skLineSegment(sketch, "E25", {"start": v(-278.64, 21) * mm, "end": v(-278.64, -106) * mm});
            skLineSegment(sketch, "E26", {"start": v(-278.64, -106) * mm, "end": v(-392.94, -106) * mm});
            skLineSegment(sketch, "E27", {"start": v(-392.94, -106) * mm, "end": v(-392.94, -918.8) * mm});
            skLineSegment(sketch, "E28", {"start": v(-392.94, -918.8) * mm, "end": v(-278.64, -918.8) * mm});
            skSolve(sketch);
        }
        {
            var Q0;
            Q0 = qSketchRegion(id + "F84", true);
            extrude(context, id + "F85", {"entities" : qUnion([Q0]), "depth" : 19.05 * mm, "offsetDistance" : 25.4 * mm});
        }
        {
            var Q0;
            Q0=makeQuery(id+"F85.opExtrude","SWEPT_BODY",BODY,{"disambiguationData":[OSD([sQuery(id+"F84.wireOp",EDGE,"E17"),sQuery(id+"F84.wireOp",EDGE,"E18"),sQuery(id+"F84.wireOp",EDGE,"E19"),sQuery(id+"F84.wireOp",EDGE,"E20"),sQuery(id+"F84.wireOp",EDGE,"E21"),sQuery(id+"F84.wireOp",EDGE,"E22"),sQuery(id+"F84.wireOp",EDGE,"E23"),sQuery(id+"F84.wireOp",EDGE,"E24"),sQuery(id+"F84.wireOp",EDGE,"E25"),sQuery(id+"F84.wireOp",EDGE,"E26"),sQuery(id+"F84.wireOp",EDGE,"E27"),sQuery(id+"F84.wireOp",EDGE,"E28")])]});
            var Q1;
            Q1=makeQuery(id+"F85.opExtrude","SWEPT_FACE",FACE,{"disambiguationData":[OSD([sQuery(id+"F84.wireOp",EDGE,"E21")])]});
            transform(context, id + "F86", {"entities" : qUnion([Q0]), "transformType" : TransformType.TRANSLATION_DISTANCE, "transformDirection" : qUnion([Q1]), "distance" : 1498.6 * mm, "makeCopy" : true});
        }
        {
            var Q0;
            Q0=makeQuery(id+"F85.opExtrude","SWEPT_BODY",BODY,{"disambiguationData":[OSD([sQuery(id+"F84.wireOp",EDGE,"E17"),sQuery(id+"F84.wireOp",EDGE,"E18"),sQuery(id+"F84.wireOp",EDGE,"E19"),sQuery(id+"F84.wireOp",EDGE,"E20"),sQuery(id+"F84.wireOp",EDGE,"E21"),sQuery(id+"F84.wireOp",EDGE,"E22"),sQuery(id+"F84.wireOp",EDGE,"E23"),sQuery(id+"F84.wireOp",EDGE,"E24"),sQuery(id+"F84.wireOp",EDGE,"E25"),sQuery(id+"F84.wireOp",EDGE,"E26"),sQuery(id+"F84.wireOp",EDGE,"E27"),sQuery(id+"F84.wireOp",EDGE,"E28")])]});
            var Q1;
            Q1=makeQuery(id+"F85.opExtrude","CAP_FACE",FACE,{"disambiguationData":[OSD([sQuery(id+"F84.wireOp",EDGE,"E17"),sQuery(id+"F84.wireOp",EDGE,"E18"),sQuery(id+"F84.wireOp",EDGE,"E19"),sQuery(id+"F84.wireOp",EDGE,"E20"),sQuery(id+"F84.wireOp",EDGE,"E21"),sQuery(id+"F84.wireOp",EDGE,"E22"),sQuery(id+"F84.wireOp",EDGE,"E23"),sQuery(id+"F84.wireOp",EDGE,"E24"),sQuery(id+"F84.wireOp",EDGE,"E25"),sQuery(id+"F84.wireOp",EDGE,"E26"),sQuery(id+"F84.wireOp",EDGE,"E27"),sQuery(id+"F84.wireOp",EDGE,"E28")])],"isStart":false});
            transform(context, id + "F87", {"entities" : qUnion([Q0]), "transformType" : TransformType.TRANSLATION_DISTANCE, "transformDirection" : qUnion([Q1]), "distance" : 539.75 * mm, "makeCopy" : true});
        }
    });
